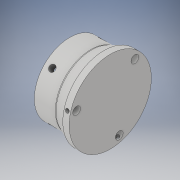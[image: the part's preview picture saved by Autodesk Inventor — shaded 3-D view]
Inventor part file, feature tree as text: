
AUTODESK INVENTOR PART (.ipt)
format: ipt  version: 2019 (Build 230136000, 136)  size: 343,552 bytes
history: native  units: in
note: dims shown in document units (in); Inventor stores cm internally (conversion verified against a paired STEP export)
features: sketch x16, extrude x11, plane x4, mirror x3, pattern_circular x2, thread x2, fillet x2, projected_geometry x2, revolve x1
ambient origin geometry x8: Origin, YZ Plane, XZ Plane, XY Plane, X Axis, Y Axis, Z Axis, Center Point
bodies: Solid1 (feature_tree), Solid2 (feature_tree)
feature tree (43):
  extrude  "Extrusion1"  Depth=1.7323in
  extrude  "Extrusion3"  Depth=1.2402in
  extrude  "Extrusion4"  Depth=1.1811in TaperAngle=0.0deg
  pattern_circular  "Circular Pattern1"  Count=4 Angle=360.0deg
  sketch  "Sketch6"  dims[d16=0.3937in d17=45.0deg]
  plane  "Work Plane1"
  extrude  "Extrusion5"  TaperAngle=45.0deg  [1 undecoded]
  plane  "Work Plane2"
  mirror  "Mirror1"
  extrude  "Extrusion6"  TaperAngle=45.0deg  [1 undecoded]
  extrude  "Extrusion7"  Depth=0.2362in TaperAngle=0.0deg
  sketch  "Sketch11"  dims[d26=0.3937in d27=0.0in d28=0.0118in]
  plane  "Work Plane3"
  extrude  "Extrusion8"  TaperAngle=45.0deg  [1 undecoded]
  thread  "Thread1"  [1 undecoded]
  mirror  "Mirror2"
  extrude  "Extrusion9"  Depth=0.3937in
  revolve  "Revolution1"  [1 undecoded]
  fillet  "Fillet1"  Radius=0.4724in
  fillet  "Fillet2"  Radius=0.0098in
  extrude  "Extrusion10"  Depth=0.4724in
  extrude  "Extrusion11"  Depth=0.3937in TaperAngle=0.0deg
  sketch  "Sketch18"  dims[d46=1.2795in]
  plane  "Work Plane4"
  sketch  "Sketch19"  dims[d47=90.0deg]
  extrude  "Extrusion12"  Depth=0.3937in TaperAngle=0.0deg
  thread  "Thread2"  [1 undecoded]
  pattern_circular  "Circular Pattern2"  [2 undecoded]
  mirror  "Mirror3"
  sketch  "Sketch2"  dims[d3=0.7874in d4=1.7323in]
  sketch  "Sketch4"  dims[d5=0.4724in d6=0.0in d9=1.2402in]
  sketch  "Sketch5"  dims[d10=0.2008in d11=1.1811in d12=0.0in d13=1.5748in d14=360.0deg]
  sketch  "Sketch7"  dims[d18=0.1181in d19=45.0deg]
  sketch  "Sketch8"  dims[d20=0.3543in d21=0.2362in d22=0.0in]
  projected_geometry  "Projected Loop1"
  sketch  "Sketch9"  dims[d23=0.8661in d24=45.0deg d25=0.2047in]
  sketch  "Sketch12"  dims[d29=0.4724in d30=0.0in d31=0.2362in d32=0.4724in d33=0.0in d34=0.0098in]
  sketch  "Sketch13"  dims[d35=45.0deg d36=0.4724in]
  sketch  "Sketch14"  dims[d37=0.1969in d38=0.3937in d39=0.0in]
  sketch  "Sketch15"  dims[d40=0.3937in d41=0.0in d42=0.1969in d43=0.0in d44=0.3937in]
  projected_geometry  "Projected Loop2"
  sketch  "Sketch17"  dims[d45=180.0deg]
  sketch  "Sketch20"  dims[d48=90.0deg d49=0.0787in d50=0.0157in d51=0.1969in d52=0.0in d53=1.0827in d54=45.0deg d55=0.2402in d56=0.1969in d57=0.0in d58=45.0deg d59=0.1969in d60=180.0deg d61=0.1181in d62=0.1181in d63=0.0in d64=1.1811in d65=360.0deg d67=0.3937in d68=0.0in]
note: 8 required parameter values undecoded (feature->parameter linkage not recoverable at this tier; creation-order binding heuristic only, values carry confidence <= 0.55)